# Revit family: Power-ModularDevices-GEWISS-90AM-TRANSFORMER_BELL_2M
name_source: partatom
category: Apparecchi elettrici
revit_build: Autodesk Revit 2016 (Build: 20161004_0715(x64)
units: mm (PartAtom-declared; Revit-internal decimal feet)

## family parameters
Condiviso = No
Host = Superficie
Mantenere orientamento annotazione = Sì
Numero OmniClass = 23.80.50.00
Punto di calcolo locali = Sì
Quota connettore circolare = Usa diametro
Taglio con vuoti quando caricato = No
Tipo di parte = Normale
Titolo OmniClass = Terminals for Power Supply

## types (6) — shared parameters
Catalogue = POWER
Catalogue Range = 90 AM
Electrocod = 140
IDF = 813d1fbe-16da-448c-b3ab-d9575e3854d7
IDT = cbcd798a-4adf-47fc-b631-f25fc000f612
Immagine tipo = GW96421.jpg
No. Chorus modules = 2
No. of modules EN 50022 = 2
Numero di poli = 1
Operation = Intermittent
Primary voltage = 230V
Produttore = GEWISS S.p.A.
Prospetto di default = 1219 mm
SEO = Transformer
Spostamento_x = -3300 mm  [stored -10.8268 ft]
Technical sheet = https://www.gewiss.com
URL = https://www.gewiss.com
Version file RFA = 18.0
carico = Altro
potenza in watt = 0 V
zero-valued in all types: Barra_DIN

## per-type parameters (varying)
| type | Descrizione | EAN code | Modello | Power | Rated power: | Secondary voltage |
| GW96421 - BELL TRANSFORMER 5VA T.P.230V T.S.12V | BELL TRANSFORMER 5VA T.P.230V T.S.12V | 8011564063709 | GW96421 | 6VA (12V) 4VA (8V) 2VA (4V) | 6 VA (12 V) 4 VA (8 V) 2 VA (4 V) | 4+8=12 V |
| GW96422 - BELL TRANSFORMER 5VA T.P.230V T.S.24V | BELL TRANSFORMER 5VA T.P.230V T.S.24V | 8011564063716 | GW96422 | 6VA (24V) 3VA (12V) | 6 VA (24 V) 3 VA (12 V) | 12+12=24 V |
| GW96423 - BELL TRANSFORMER 10VA T.P.230V T.S.12V | BELL TRANSFORMER 10VA T.P.230V T.S.12V | 8011564063723 | GW96423 | 10VA (12V)/6,6VA (8V)/3,3VA (4V) | 10 VA (12 V)/6.6 VA (8 V)/3.3 VA (4 V) | 4+8=12 V |
| GW96424 - BELL TRANSFORMER 10VA T.P.230V T.S.24V | BELL TRANSFORMER 10VA T.P.230V T.S.24V | 8011564063730 | GW96424 | 10VA (24V)/5VA (12V) | 10 VA (24 V)/5 VA (12 V) | 12+12=24 V |
| GW96426 - BELL TRANSFORMER 15VA T.P.230V T.S.24V | BELL TRANSFORMER 15VA T.P.230V T.S.24V | 8011564063754 | GW96426 | 15VA (24V)/7,5VA(12V) | 15 VA (24 V)/7.5 VA(12 V) | 12+12=24 V |
| GW96425 - BELL TRANSFORMER 15VA T.P.230V T.S.12V | BELL TRANSFORMER 15VA T.P.230V T.S.12V | 8011564063747 | GW96425 | 15VA (12V)/10VA (8V)/5VA (4V) | 15 VA (12 V)/10 VA (8 V)/5 VA (4 V) | 4+8=12 V |

note: [stored X ft] marks values corroborated as IEEE doubles in the binary element streams (Revit-internal decimal feet)
